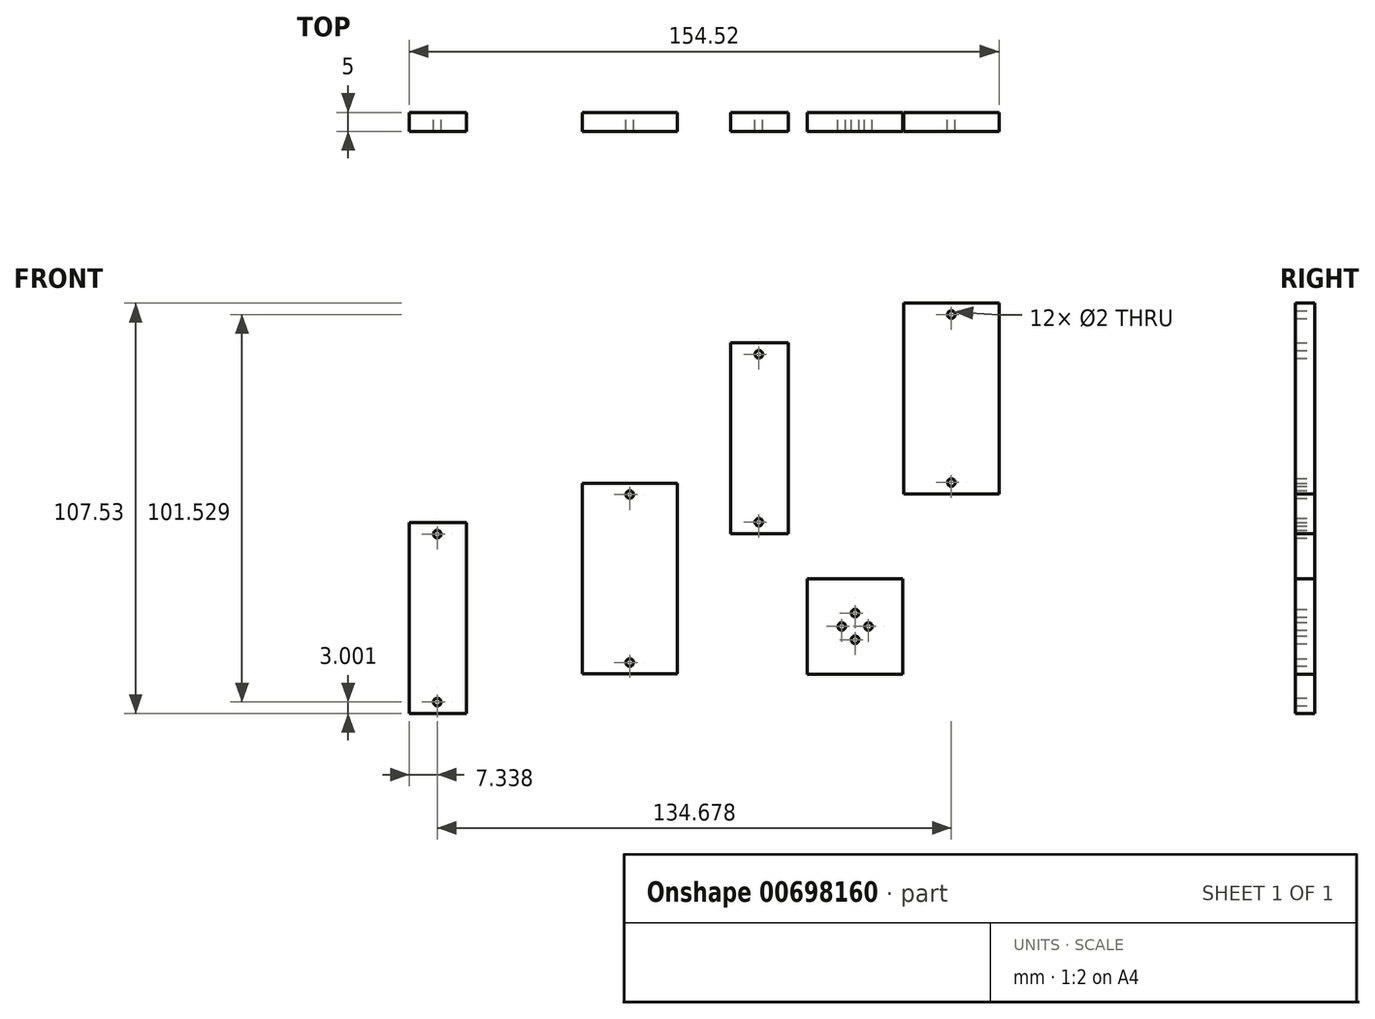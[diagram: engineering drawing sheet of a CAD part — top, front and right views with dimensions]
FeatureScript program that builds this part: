
annotation { "Feature Type Name" : "Feature", "Feature Type Description" : "" }
export const myFeature = defineFeature(function(context is Context, id is Id, definition is map)
    precondition{}
    {
        {
            var Q0;
            Q0=qCreatedBy(makeId("Front.planeOp"),FACE);
            var sketch = newSketch(context, id + "F0", { "sketchPlane" : qUnion([Q0])});
            skLineSegment(sketch, "E0.bottom", {"start": v(-7.33, 0) * mm, "end": v(7.67, 0) * mm});
            skLineSegment(sketch, "E0.top", {"start": v(-7.33, 50) * mm, "end": v(7.67, 50) * mm});
            skLineSegment(sketch, "E0.left", {"start": v(-7.33, 0) * mm, "end": v(-7.33, 50) * mm});
            skLineSegment(sketch, "E0.right", {"start": v(7.67, 0) * mm, "end": v(7.67, 50) * mm});
            skCircle(sketch, "E1", {"center": v(0, 47) * mm, "radius": 1 * mm});
            skCircle(sketch, "E2", {"center": v(0, 3) * mm, "radius": 1 * mm});
            skLineSegment(sketch, "E3.bottom", {"start": v(37.94, 10.38) * mm, "end": v(62.94, 10.38) * mm});
            skLineSegment(sketch, "E3.top", {"start": v(37.94, 60.38) * mm, "end": v(62.94, 60.38) * mm});
            skLineSegment(sketch, "E3.left", {"start": v(37.94, 10.38) * mm, "end": v(37.94, 60.38) * mm});
            skLineSegment(sketch, "E3.right", {"start": v(62.94, 10.38) * mm, "end": v(62.94, 60.38) * mm});
            skCircle(sketch, "E4", {"center": v(50.44, 57.38) * mm, "radius": 1 * mm});
            skCircle(sketch, "E5", {"center": v(50.44, 13.38) * mm, "radius": 1 * mm});
            skLineSegment(sketch, "E6.bottom", {"start": v(-91.58, -47.15) * mm, "end": v(-76.58, -47.15) * mm});
            skLineSegment(sketch, "E6.top", {"start": v(-91.58, 2.85) * mm, "end": v(-76.58, 2.85) * mm});
            skLineSegment(sketch, "E6.left", {"start": v(-91.58, -47.15) * mm, "end": v(-91.58, 2.85) * mm});
            skLineSegment(sketch, "E6.right", {"start": v(-76.58, -47.15) * mm, "end": v(-76.58, 2.85) * mm});
            skCircle(sketch, "E7", {"center": v(-84.24, -0.15) * mm, "radius": 1 * mm});
            skCircle(sketch, "E8", {"center": v(-84.24, -44.15) * mm, "radius": 1 * mm});
            skLineSegment(sketch, "E9.bottom", {"start": v(-46.3, -36.77) * mm, "end": v(-21.3, -36.77) * mm});
            skLineSegment(sketch, "E9.top", {"start": v(-46.3, 13.23) * mm, "end": v(-21.3, 13.23) * mm});
            skLineSegment(sketch, "E9.left", {"start": v(-46.3, -36.77) * mm, "end": v(-46.3, 13.23) * mm});
            skLineSegment(sketch, "E9.right", {"start": v(-21.3, -36.77) * mm, "end": v(-21.3, 13.23) * mm});
            skCircle(sketch, "E10", {"center": v(-33.8, 10.23) * mm, "radius": 1 * mm});
            skCircle(sketch, "E11", {"center": v(-33.8, -33.77) * mm, "radius": 1 * mm});
            skLineSegment(sketch, "E12.bottom", {"start": v(12.73, -11.83) * mm, "end": v(37.73, -11.83) * mm});
            skLineSegment(sketch, "E12.top", {"start": v(12.73, -36.83) * mm, "end": v(37.73, -36.83) * mm});
            skLineSegment(sketch, "E12.left", {"start": v(12.73, -11.83) * mm, "end": v(12.73, -36.83) * mm});
            skLineSegment(sketch, "E12.right", {"start": v(37.73, -11.83) * mm, "end": v(37.73, -36.83) * mm});
            skCircle(sketch, "E13", {"center": v(25.23, -20.83) * mm, "radius": 1 * mm});
            skCircle(sketch, "E14", {"center": v(21.73, -24.33) * mm, "radius": 1 * mm});
            skCircle(sketch, "E15", {"center": v(28.73, -24.33) * mm, "radius": 1 * mm});
            skCircle(sketch, "E16", {"center": v(25.23, -27.83) * mm, "radius": 1 * mm});
            skSolve(sketch);
        }
        {
            var Q0;
            Q0=makeQuery(id+"F0.imprint","IMPRINT",FACE,{"disambiguationData":[TD([[makeQuery(id+"F0.imprint","IMPRINT",EDGE,{"derivedFrom":sQuery(id+"F0.wireOp",EDGE,"E0.bottom")}),1.0]])]});
            var Q1;
            Q1=makeQuery(id+"F0.imprint","IMPRINT",FACE,{"disambiguationData":[TD([[makeQuery(id+"F0.imprint","IMPRINT",EDGE,{"derivedFrom":sQuery(id+"F0.wireOp",EDGE,"7faf0409-18d8-4add-b0b0-ebf9e8c7e117.bottom")}),1.0]])]});
            var Q2;
            Q2=makeQuery(id+"F0.imprint","IMPRINT",FACE,{"disambiguationData":[TD([[makeQuery(id+"F0.imprint","IMPRINT",EDGE,{"derivedFrom":sQuery(id+"F0.wireOp",EDGE,"4906e261-39f9-437f-9cc4-5b27bfd78ccf.bottom")}),1.0]])]});
            var Q3;
            Q3=makeQuery(id+"F0.imprint","IMPRINT",FACE,{"disambiguationData":[TD([[makeQuery(id+"F0.imprint","IMPRINT",EDGE,{"derivedFrom":sQuery(id+"F0.wireOp",EDGE,"b8d77748-c16d-4c90-a04a-ca2a659a7044.bottom")}),1.0]])]});
            extrude(context, id + "F1", {"entities" : qUnion([Q0, Q1, Q2, Q3]), "depth" : 5 * mm, "offsetDistance" : 25 * mm});
        }
        {
            var Q0;
            Q0 = qSketchRegion(id + "F0", true);
            extrude(context, id + "F2", {"entities" : qUnion([Q0]), "operationType" : NewBodyOperationType.ADD, "depth" : 5 * mm, "offsetDistance" : 25 * mm});
        }
    });
